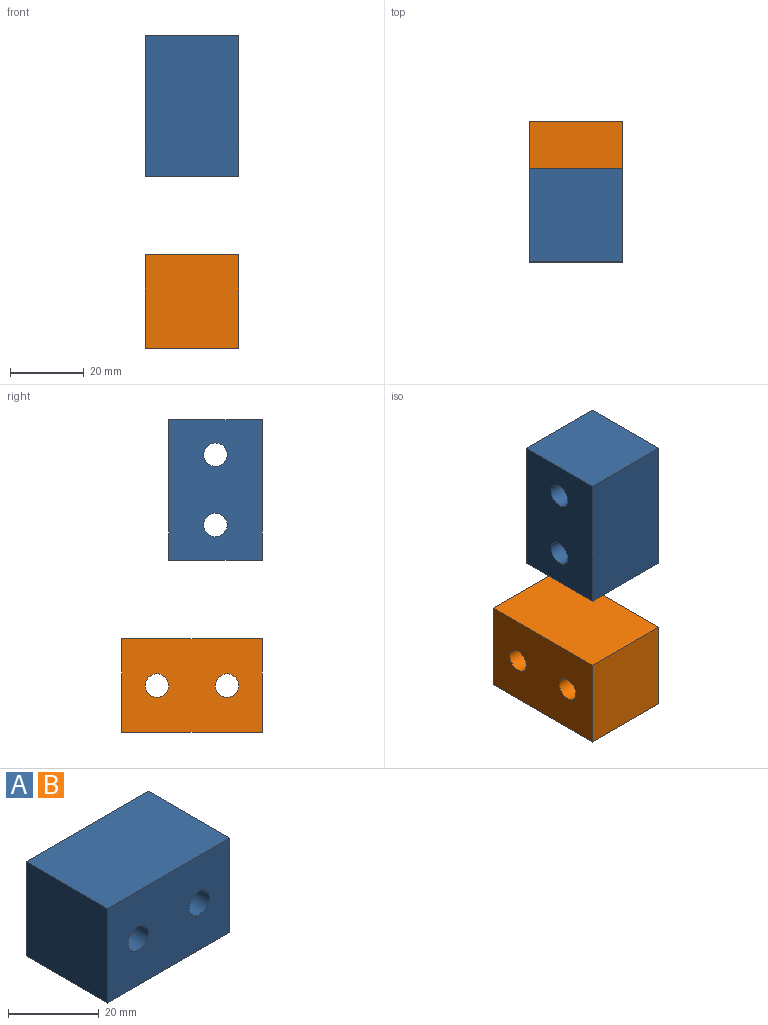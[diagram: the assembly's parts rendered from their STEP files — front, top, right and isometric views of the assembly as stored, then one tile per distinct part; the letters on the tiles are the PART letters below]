
ASSEMBLY  parts=2 mates=1
PART A: 8 faces, bbox 38.1x25.4x25.4 mm
  f0: plane 25.4x25.4mm, normal (1,0,0), area 645.2mm2, adj f1,f3,f4,f5
  f1: plane 38.1x25.4mm, normal (0,1,0), area 904.4mm2, adj f0,f2,f4,f5,f6,f7
  f2: plane 25.4x25.4mm, normal (-1,0,0), area 645.2mm2, adj f1,f3,f4,f5
  f3: plane 38.1x25.4mm, normal (0,-1,0), area 904.4mm2, adj f0,f2,f4,f5,f6,f7
  f4: plane 38.1x25.4mm, normal (0,0,1), area 967.7mm2, adj f0,f1,f2,f3
  f5: plane 38.1x25.4mm, normal (0,0,-1), area 967.7mm2, adj f0,f1,f2,f3
  f6: cylinder r=3.17mm len=25.4mm, axis (0,-1,0), area 506.7mm2, adj f1,f3
  f7: cylinder r=3.17mm len=25.4mm, axis (0,-1,0), area 506.7mm2, adj f1,f3
PART B: same geometry as A
PLACE A rot(axis=(-0.58,0.58,0.58),120deg) t=(-12.7,-20.17,5.88)mm
PLACE B rot(axis=(0.71,-0.71,0),180deg) t=(-12.7,-1.12,-34.49)mm
MATE slider B.f5 <-> A.f2  axis (0,0,1) through (-25.4,-20.17,-34.49)mm
